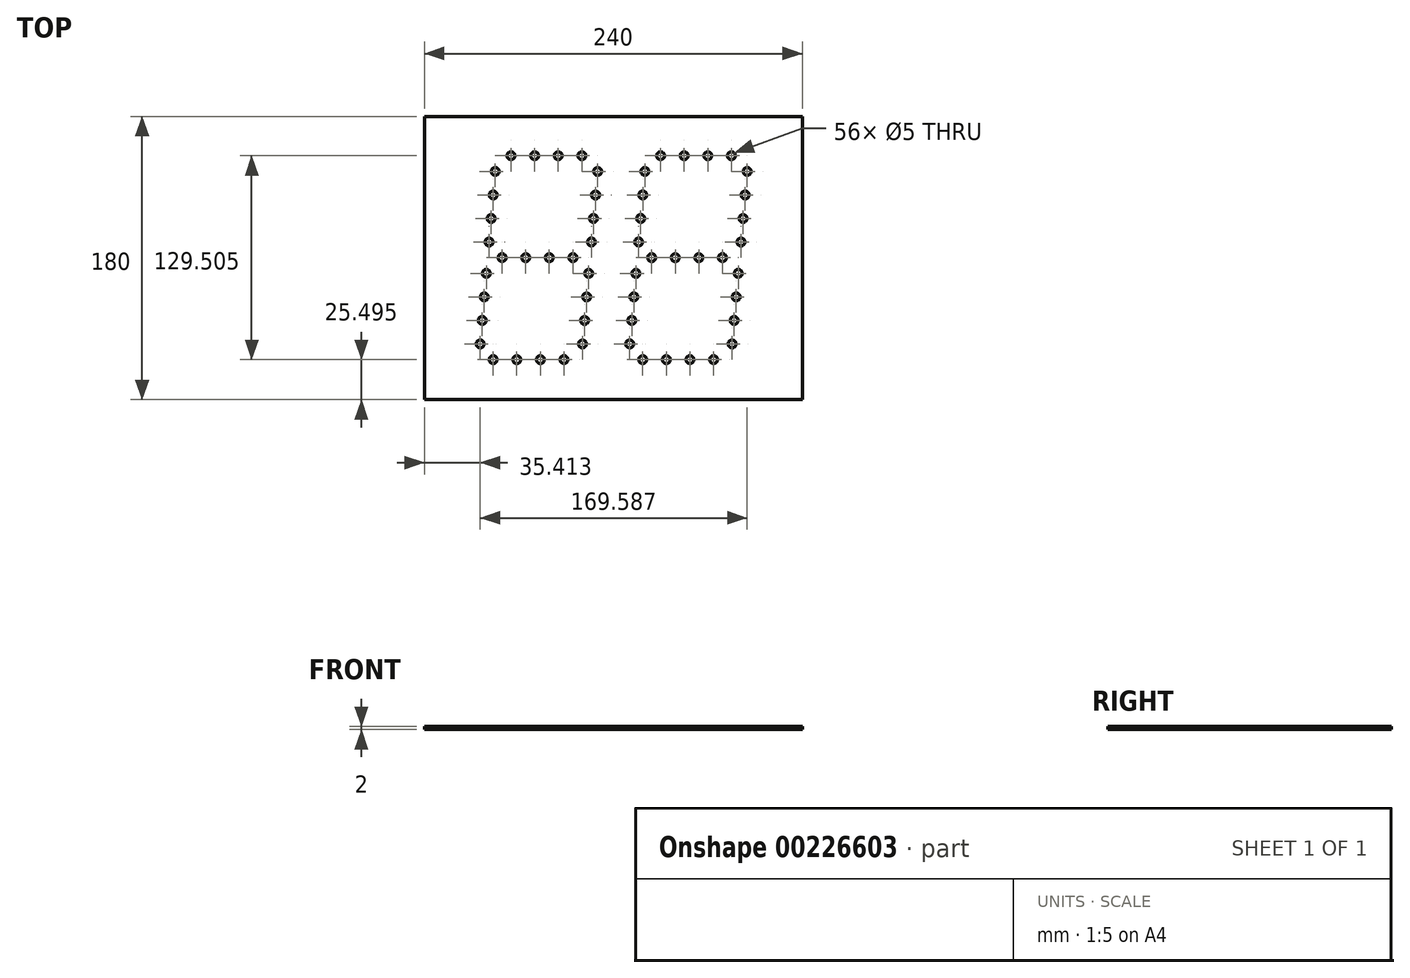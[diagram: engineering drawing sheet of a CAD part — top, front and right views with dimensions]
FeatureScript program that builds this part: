
annotation { "Feature Type Name" : "Feature", "Feature Type Description" : "" }
export const myFeature = defineFeature(function(context is Context, id is Id, definition is map)
    precondition{}
    {
        {
            var Q0;
            Q0=qCreatedBy(makeId("Top.planeOp"),FACE);
            var sketch = newSketch(context, id + "F0", { "sketchPlane" : qUnion([Q0])});
            skLineSegment(sketch, "E0.bottom", {"start": v(-120, 90) * mm, "end": v(120, 90) * mm});
            skLineSegment(sketch, "E0.top", {"start": v(-120, -90) * mm, "end": v(120, -90) * mm});
            skLineSegment(sketch, "E0.left", {"start": v(-120, 90) * mm, "end": v(-120, -90) * mm});
            skLineSegment(sketch, "E0.right", {"start": v(120, 90) * mm, "end": v(120, -90) * mm});
            skSolve(sketch);
        }
        {
            var Q0;
            Q0 = qSketchRegion(id + "F0", true);
            extrude(context, id + "F1", {"entities" : qUnion([Q0]), "endBound" : BoundingType.SYMMETRIC, "depth" : 2 * mm});
        }
        {
            var Q0;
            Q0=makeQuery(id+"F1.opExtrude","CAP_FACE",FACE,{"disambiguationData":[OSD([sQuery(id+"F0.wireOp",EDGE,"E0.bottom"),sQuery(id+"F0.wireOp",EDGE,"E0.top"),sQuery(id+"F0.wireOp",EDGE,"E0.left"),sQuery(id+"F0.wireOp",EDGE,"E0.right")])],"isStart":false});
            var sketch = newSketch(context, id + "F2", { "sketchPlane" : qUnion([Q0])});
            skCircle(sketch, "E1.3.0.0", {"center": v(-20, 65) * mm, "radius": 2.5 * mm});
            skCircle(sketch, "E2.0.1.0", {"center": v(-25.67, 0.25) * mm, "radius": 2.5 * mm});
            skCircle(sketch, "E2.0.2.0", {"center": v(-31.33, -64.5) * mm, "radius": 2.5 * mm});
            skCircle(sketch, "E2.1.0.0", {"center": v(-35, 65) * mm, "radius": 2.5 * mm});
            skCircle(sketch, "E2.1.1.0", {"center": v(-40.67, 0.25) * mm, "radius": 2.5 * mm});
            skCircle(sketch, "E2.1.2.0", {"center": v(-46.33, -64.5) * mm, "radius": 2.5 * mm});
            skCircle(sketch, "E2.2.0.0", {"center": v(-50, 65) * mm, "radius": 2.5 * mm});
            skCircle(sketch, "E2.2.1.0", {"center": v(-55.67, 0.25) * mm, "radius": 2.5 * mm});
            skCircle(sketch, "E2.2.2.0", {"center": v(-61.33, -64.5) * mm, "radius": 2.5 * mm});
            skCircle(sketch, "E2.3.0.0", {"center": v(-65, 65) * mm, "radius": 2.5 * mm});
            skCircle(sketch, "E2.3.1.0", {"center": v(-70.67, 0.25) * mm, "radius": 2.5 * mm});
            skCircle(sketch, "E2.3.2.0", {"center": v(-76.33, -64.5) * mm, "radius": 2.5 * mm});
            skLineSegment(sketch, "E2.direction1", {"start": v(-20, 65) * mm, "end": v(-35, 65) * mm, "construction": true});
            skLineSegment(sketch, "E2.direction2", {"start": v(-20, 65) * mm, "end": v(-25.67, 0.25) * mm, "construction": true});
            skCircle(sketch, "E3", {"center": v(-75, 55) * mm, "radius": 2.5 * mm});
            skCircle(sketch, "E4.1.0.0", {"center": v(-76.3, 40.06) * mm, "radius": 2.5 * mm});
            skCircle(sketch, "E4.2.0.0", {"center": v(-77.61, 25.11) * mm, "radius": 2.5 * mm});
            skCircle(sketch, "E4.3.0.0", {"center": v(-78.92, 10.17) * mm, "radius": 2.5 * mm});
            skLineSegment(sketch, "E4.direction1", {"start": v(-75, 55) * mm, "end": v(-76.3, 40.06) * mm, "construction": true});
            skCircle(sketch, "E5.1.0.0", {"center": v(-80.67, -9.75) * mm, "radius": 2.5 * mm});
            skCircle(sketch, "E5.1.0.1", {"center": v(-81.97, -24.7) * mm, "radius": 2.5 * mm});
            skCircle(sketch, "E5.1.0.2", {"center": v(-83.28, -39.64) * mm, "radius": 2.5 * mm});
            skCircle(sketch, "E5.1.0.3", {"center": v(-84.59, -54.58) * mm, "radius": 2.5 * mm});
            skLineSegment(sketch, "E5.direction1", {"start": v(-78.92, 10.17) * mm, "end": v(-84.59, -54.58) * mm, "construction": true});
            skCircle(sketch, "E6.1.0.0", {"center": v(-10, 55) * mm, "radius": 2.5 * mm});
            skCircle(sketch, "E6.1.0.1", {"center": v(-11.3, 40.06) * mm, "radius": 2.5 * mm});
            skCircle(sketch, "E6.1.0.2", {"center": v(-12.61, 25.11) * mm, "radius": 2.5 * mm});
            skCircle(sketch, "E6.1.0.3", {"center": v(-13.92, 10.17) * mm, "radius": 2.5 * mm});
            skCircle(sketch, "E6.1.0.4", {"center": v(-15.67, -9.75) * mm, "radius": 2.5 * mm});
            skCircle(sketch, "E6.1.0.5", {"center": v(-16.97, -24.7) * mm, "radius": 2.5 * mm});
            skCircle(sketch, "E6.1.0.6", {"center": v(-18.28, -39.64) * mm, "radius": 2.5 * mm});
            skCircle(sketch, "E6.1.0.7", {"center": v(-19.59, -54.58) * mm, "radius": 2.5 * mm});
            skLineSegment(sketch, "E6.direction1", {"start": v(-84.59, -54.58) * mm, "end": v(-19.59, -54.58) * mm, "construction": true});
            skLineSegment(sketch, "E7.1.0.0", {"start": v(16.08, 10.17) * mm, "end": v(10.41, -54.58) * mm, "construction": true});
            skCircle(sketch, "E7.1.0.1", {"center": v(30, 65) * mm, "radius": 2.5 * mm});
            skCircle(sketch, "E7.1.0.2", {"center": v(39.33, 0.25) * mm, "radius": 2.5 * mm});
            skLineSegment(sketch, "E7.1.0.3", {"start": v(10.41, -54.58) * mm, "end": v(75.41, -54.58) * mm, "construction": true});
            skCircle(sketch, "E7.1.0.4", {"center": v(16.08, 10.17) * mm, "radius": 2.5 * mm});
            skLineSegment(sketch, "E7.1.0.5", {"start": v(20, 55) * mm, "end": v(18.7, 40.06) * mm, "construction": true});
            skCircle(sketch, "E7.1.0.6", {"center": v(24.33, 0.25) * mm, "radius": 2.5 * mm});
            skCircle(sketch, "E7.1.0.7", {"center": v(78.03, -24.7) * mm, "radius": 2.5 * mm});
            skCircle(sketch, "E7.1.0.8", {"center": v(81.08, 10.17) * mm, "radius": 2.5 * mm});
            skLineSegment(sketch, "E7.1.0.9", {"start": v(75, 65) * mm, "end": v(60, 65) * mm, "construction": true});
            skCircle(sketch, "E7.1.0.10", {"center": v(79.33, -9.75) * mm, "radius": 2.5 * mm});
            skCircle(sketch, "E7.1.0.11", {"center": v(85, 55) * mm, "radius": 2.5 * mm});
            skCircle(sketch, "E7.1.0.12", {"center": v(45, 65) * mm, "radius": 2.5 * mm});
            skCircle(sketch, "E7.1.0.13", {"center": v(48.67, -64.5) * mm, "radius": 2.5 * mm});
            skCircle(sketch, "E7.1.0.14", {"center": v(20, 55) * mm, "radius": 2.5 * mm});
            skLineSegment(sketch, "E7.1.0.15", {"start": v(75, 65) * mm, "end": v(69.33, 0.25) * mm, "construction": true});
            skCircle(sketch, "E7.1.0.16", {"center": v(54.33, 0.25) * mm, "radius": 2.5 * mm});
            skCircle(sketch, "E7.1.0.17", {"center": v(60, 65) * mm, "radius": 2.5 * mm});
            skCircle(sketch, "E7.1.0.18", {"center": v(75, 65) * mm, "radius": 2.5 * mm});
            skCircle(sketch, "E7.1.0.19", {"center": v(69.33, 0.25) * mm, "radius": 2.5 * mm});
            skCircle(sketch, "E7.1.0.20", {"center": v(83.7, 40.06) * mm, "radius": 2.5 * mm});
            skCircle(sketch, "E7.1.0.21", {"center": v(18.67, -64.5) * mm, "radius": 2.5 * mm});
            skCircle(sketch, "E7.1.0.22", {"center": v(13.03, -24.7) * mm, "radius": 2.5 * mm});
            skCircle(sketch, "E7.1.0.23", {"center": v(17.39, 25.11) * mm, "radius": 2.5 * mm});
            skCircle(sketch, "E7.1.0.24", {"center": v(33.67, -64.5) * mm, "radius": 2.5 * mm});
            skCircle(sketch, "E7.1.0.25", {"center": v(14.33, -9.75) * mm, "radius": 2.5 * mm});
            skCircle(sketch, "E7.1.0.26", {"center": v(82.39, 25.11) * mm, "radius": 2.5 * mm});
            skCircle(sketch, "E7.1.0.27", {"center": v(76.72, -39.64) * mm, "radius": 2.5 * mm});
            skCircle(sketch, "E7.1.0.28", {"center": v(11.72, -39.64) * mm, "radius": 2.5 * mm});
            skCircle(sketch, "E7.1.0.29", {"center": v(63.67, -64.5) * mm, "radius": 2.5 * mm});
            skCircle(sketch, "E7.1.0.30", {"center": v(75.41, -54.58) * mm, "radius": 2.5 * mm});
            skCircle(sketch, "E7.1.0.31", {"center": v(18.7, 40.06) * mm, "radius": 2.5 * mm});
            skCircle(sketch, "E7.1.0.32", {"center": v(10.41, -54.58) * mm, "radius": 2.5 * mm});
            skLineSegment(sketch, "E7.direction1", {"start": v(-76.33, -64.5) * mm, "end": v(18.67, -64.5) * mm, "construction": true});
            skSolve(sketch);
        }
        {
            var Q0;
            Q0 = qSketchRegion(id + "F2", true);
            extrude(context, id + "F3", {"entities" : qUnion([Q0]), "operationType" : NewBodyOperationType.REMOVE, "endBound" : BoundingType.THROUGH_ALL, "oppositeDirection" : true, "depth" : 25 * mm});
        }
    });
